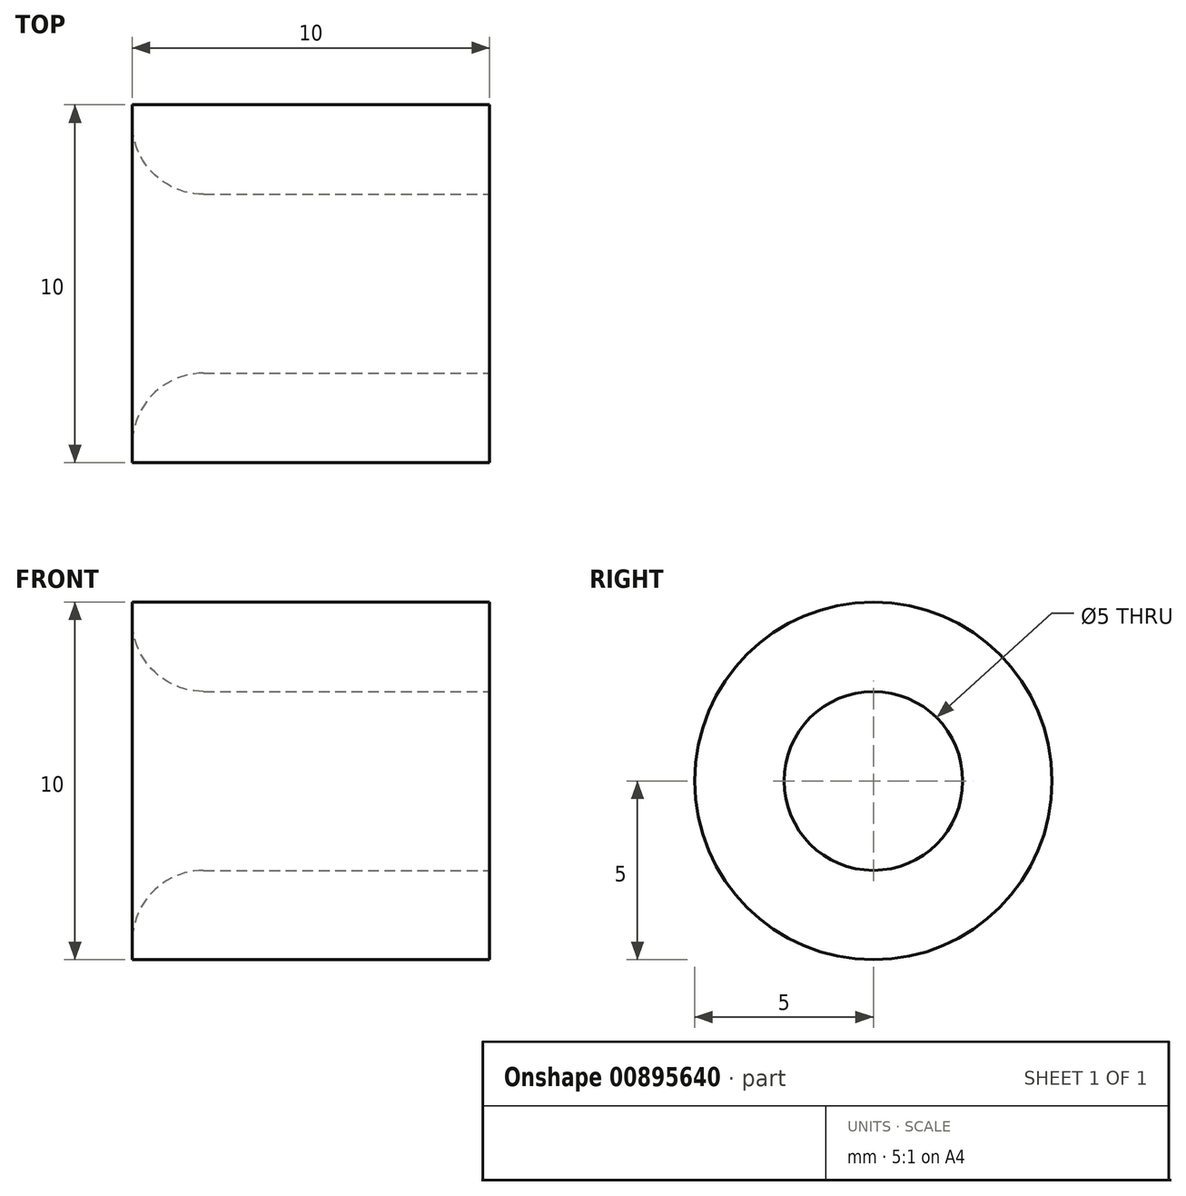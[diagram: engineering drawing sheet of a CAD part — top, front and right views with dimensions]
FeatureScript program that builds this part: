
annotation { "Feature Type Name" : "Feature", "Feature Type Description" : "" }
export const myFeature = defineFeature(function(context is Context, id is Id, definition is map)
    precondition{}
    {
        {
            var Q0;
            Q0=qCreatedBy(makeId("Right.planeOp"),FACE);
            var sketch = newSketch(context, id + "F0", { "sketchPlane" : qUnion([Q0])});
            skCircle(sketch, "E0", {"center": v(0, 0) * mm, "radius": 5 * mm});
            skSolve(sketch);
        }
        {
            var Q0;
            Q0 = qSketchRegion(id + "F0", true);
            extrude(context, id + "F1", {"entities" : qUnion([Q0]), "endBound" : BoundingType.SYMMETRIC, "depth" : 10 * mm, "offsetDistance" : 25 * mm});
        }
        {
            var Q0;
            Q0=makeQuery(id+"F1.opExtrude","CAP_FACE",FACE,{"disambiguationData":[OSD([sQuery(id+"F0.wireOp",EDGE,"E0")])],"isStart":false});
            var sketch = newSketch(context, id + "F2", { "sketchPlane" : qUnion([Q0])});
            skCircle(sketch, "E1", {"center": v(0, 0) * mm, "radius": 2.5 * mm});
            skSolve(sketch);
        }
        {
            var Q0;
            Q0 = qSketchRegion(id + "F2", true);
            extrude(context, id + "F3", {"entities" : qUnion([Q0]), "operationType" : NewBodyOperationType.REMOVE, "oppositeDirection" : true, "depth" : 25 * mm, "offsetDistance" : 25 * mm});
        }
        {
            var Q0;
            Q0=makeQuery(id+"F3.boolean.opBoolean","COPY",EDGE,{"derivedFrom":makeQuery(id+"F3.opExtrude","CAP_EDGE",EDGE,{"disambiguationData":[OSD([sQuery(id+"F2.wireOp",EDGE,"E1")])],"isStart":true})});
            var Q1;
            Q1=makeQuery(id+"F3.boolean.opBoolean","INTERSECT",EDGE,{"derivedFrom":[makeQuery(id+"F1.opExtrude","CAP_FACE",FACE,{"disambiguationData":[OSD([sQuery(id+"F0.wireOp",EDGE,"E0")])],"isStart":true}),makeQuery(id+"F3.opExtrude","SWEPT_FACE",FACE,{"disambiguationData":[OSD([sQuery(id+"F2.wireOp",EDGE,"E1")])]})]});
            fillet(context, id + "F4", {"entities" : qUnion([Q0, Q1]), "radius" : 2 * mm, "tangentPropagation" : true, "allowEdgeOverflow" : false});
        }
    });
